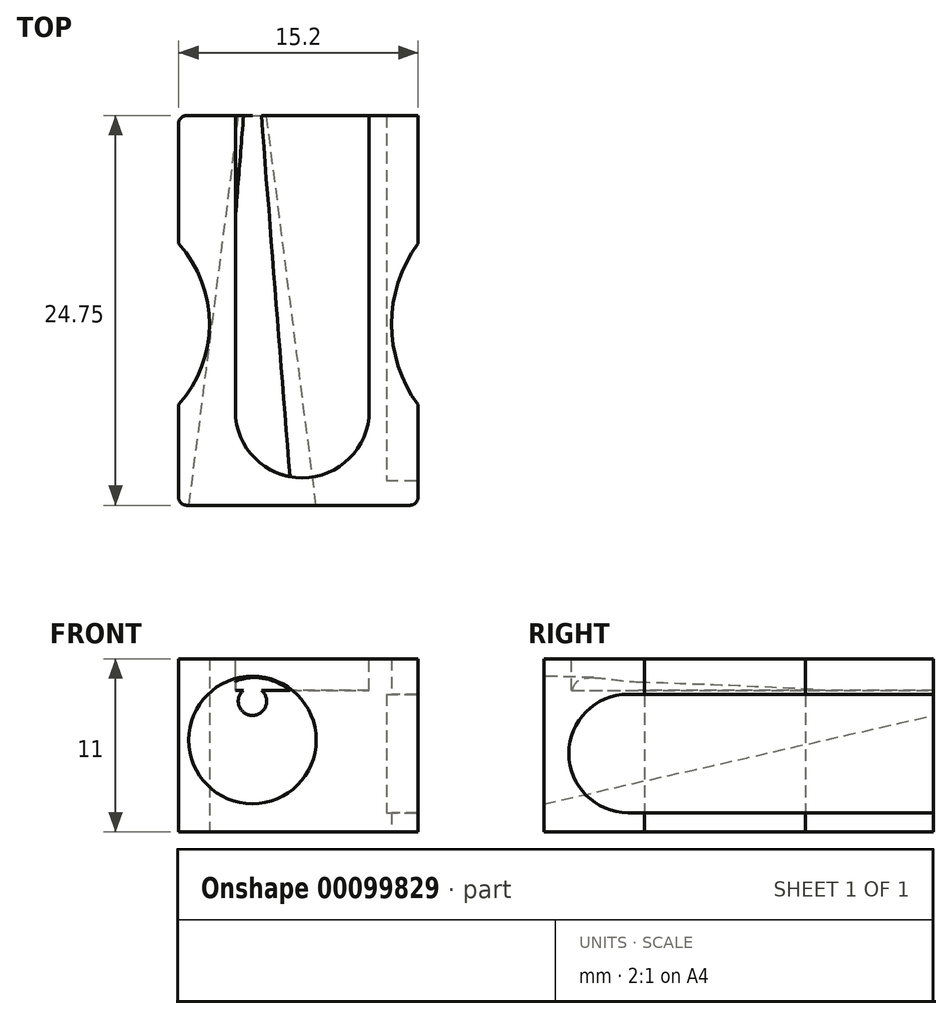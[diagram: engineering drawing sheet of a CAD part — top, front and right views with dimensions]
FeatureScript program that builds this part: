
annotation { "Feature Type Name" : "Feature", "Feature Type Description" : "" }
export const myFeature = defineFeature(function(context is Context, id is Id, definition is map)
    precondition{}
    {
        {
            var Q0;
            Q0=qCreatedBy(makeId("Top.planeOp"),FACE);
            var sketch = newSketch(context, id + "F0", { "sketchPlane" : qUnion([Q0])});
            skLineSegment(sketch, "E0", {"start": v(-7.6, 0) * mm, "end": v(7.6, 0) * mm});
            skLineSegment(sketch, "E1", {"start": v(7.6, 24.75) * mm, "end": v(-7.6, 24.75) * mm});
            skArc(sketch, "E2", {"start": v(7.6, 16.6) * mm, "mid": v(5.93, 11.5) * mm, "end": v(7.6, 6.4) * mm});
            skArc(sketch, "E3", {"start": v(-7.6, 6.4) * mm, "mid": v(-5.65, 11.5) * mm, "end": v(-7.6, 16.6) * mm});
            skLineSegment(sketch, "E4", {"start": v(-7.6, 24.75) * mm, "end": v(-7.6, 16.6) * mm});
            skLineSegment(sketch, "E5", {"start": v(-7.6, 6.4) * mm, "end": v(-7.6, 0) * mm});
            skLineSegment(sketch, "E6", {"start": v(7.6, 24.75) * mm, "end": v(7.6, 16.6) * mm});
            skLineSegment(sketch, "E7", {"start": v(7.6, 6.4) * mm, "end": v(7.6, 0) * mm});
            skSolve(sketch);
        }
        {
            var Q0;
            Q0 = qSketchRegion(id + "F0", true);
            var Q1;
            Q1=makeQuery(id+"F0.imprint","IMPRINT",FACE,{"disambiguationData":[TD([[makeQuery(id+"F0.imprint","IMPRINT",EDGE,{"derivedFrom":sQuery(id+"F0.wireOp",EDGE,"E0")}),1.0]])]});
            extrude(context, id + "F1", {"entities" : qUnion([Q0, Q1]), "depth" : 11 * mm});
        }
        {
            var Q0;
            Q0=makeQuery(id+"F1.opExtrude","CAP_FACE",FACE,{"disambiguationData":[OSD([sQuery(id+"F0.wireOp",EDGE,"E0"),sQuery(id+"F0.wireOp",EDGE,"CH1Bz3xv-YDNb-fB7E-m70Z-ND1As7hxYgC0"),sQuery(id+"F0.wireOp",EDGE,"E1"),sQuery(id+"F0.wireOp",EDGE,"xgEUE1xi-ovgt-coFG-tonh-Vv3ERaxNFuPz")])],"isStart":false});
            var sketch = newSketch(context, id + "F2", { "sketchPlane" : qUnion([Q0])});
            skLineSegment(sketch, "E8", {"start": v(-4, 24.75) * mm, "end": v(-4, 6) * mm});
            skLineSegment(sketch, "E9", {"start": v(4.5, 24.75) * mm, "end": v(4.5, 6) * mm});
            skArc(sketch, "E10", {"start": v(-4, 6) * mm, "mid": v(0.25, 1.74) * mm, "end": v(4.5, 6) * mm});
            skSolve(sketch);
        }
        {
            var Q0;
            {var subQ0=sQuery(id+"F2.wireOp",EDGE,"E8");Q0=makeQuery(id+"F2.imprint","IMPRINT",FACE,{"disambiguationData":[TD([[makeQuery(id+"F2.imprint","IMPRINT",EDGE,{"derivedFrom":subQ0}),1.0]])]});}
            extrude(context, id + "F3", {"entities" : qUnion([Q0]), "operationType" : NewBodyOperationType.REMOVE, "oppositeDirection" : true, "depth" : 2 * mm});
        }
        {
            var Q0;
            Q0=qCreatedBy(makeId("Front.planeOp"),FACE);
            cPlane(context, id + "F4", {"entities" : qUnion([Q0]), "cplaneType" : CPlaneType.OFFSET, "offset" : 24.75 * mm, "oppositeDirection" : true, "width" : 150 * mm, "height" : 150 * mm});
        }
        {
            var Q0;
            Q0=makeQuery(id+"F1.opExtrude","SWEPT_FACE",FACE,{"disambiguationData":[OSD([sQuery(id+"F0.wireOp",EDGE,"E0")])]});
            var sketch = newSketch(context, id + "F5", { "sketchPlane" : qUnion([Q0])});
            skCircle(sketch, "E11", {"center": v(-2.91, 5.84) * mm, "radius": 4.05 * mm});
            skSolve(sketch);
        }
        {
            var Q0;
            Q0=qCreatedBy(id+"F4.planeOp",FACE);
            var sketch = newSketch(context, id + "F6", { "sketchPlane" : qUnion([Q0])});
            skCircle(sketch, "E12", {"center": v(-2.91, 8.3) * mm, "radius": 0.9 * mm});
            skSolve(sketch);
        }
        {
            var Q1;
            Q1=makeQuery(id+"F5.imprint","IMPRINT",FACE,{"disambiguationData":[TD([[makeQuery(id+"F5.imprint","IMPRINT",EDGE,{"derivedFrom":sQuery(id+"F5.wireOp",EDGE,"E11")}),1.0]])]});
            var Q2;
            Q2=makeQuery(id+"F6.imprint","IMPRINT",FACE,{"disambiguationData":[TD([[makeQuery(id+"F6.imprint","IMPRINT",EDGE,{"derivedFrom":sQuery(id+"F6.wireOp",EDGE,"E12")}),1.0]])]});
            loft(context, id + "F7", {"operationType" : NewBodyOperationType.REMOVE, "sheetProfilesArray" : [{ "sheetProfileEntities" : qUnion([Q1]) }, { "sheetProfileEntities" : qUnion([Q2]) }]});
        }
        {
            var Q0;
            Q0=makeQuery(id+"F1.opExtrude","SWEPT_EDGE",EDGE,{"disambiguationData":[OSD([sQuery(id+"F0.wireOp",EDGE,"E0"),sQuery(id+"F0.wireOp",EDGE,"E5")])]});
            var Q1;
            Q1=makeQuery(id+"F1.opExtrude","SWEPT_EDGE",EDGE,{"disambiguationData":[OSD([sQuery(id+"F0.wireOp",EDGE,"E1"),sQuery(id+"F0.wireOp",EDGE,"E4")])]});
            var Q2;
            Q2=makeQuery(id+"F1.opExtrude","SWEPT_EDGE",EDGE,{"disambiguationData":[OSD([sQuery(id+"F0.wireOp",EDGE,"E0"),sQuery(id+"F0.wireOp",EDGE,"E7")])]});
            fillet(context, id + "F8", {"entities" : qUnion([Q0, Q1, Q2]), "radius" : 0.5 * mm, "tangentPropagation" : true, "allowEdgeOverflow" : false});
        }
        {
            var Q0;
            Q0=makeQuery(id+"F1.opExtrude","SWEPT_FACE",FACE,{"disambiguationData":[OSD([sQuery(id+"F0.wireOp",EDGE,"E6"),sQuery(id+"F0.wireOp",EDGE,"E7"),sQuery(id+"F0.wireOp",EDGE,"jYAzOSRn-kvyj-A9Oq-DmZ8-IOtMs528JoDm")])]});
            var sketch = newSketch(context, id + "F9", { "sketchPlane" : qUnion([Q0])});
            skLineSegment(sketch, "E13", {"start": v(24.75, 1.22) * mm, "end": v(5.34, 1.22) * mm});
            skArc(sketch, "E14", {"start": v(5.34, 8.74) * mm, "mid": v(1.58, 4.98) * mm, "end": v(5.34, 1.22) * mm});
            skLineSegment(sketch, "E15", {"start": v(5.34, 8.74) * mm, "end": v(24.75, 8.74) * mm});
            skSolve(sketch);
        }
        {
            var Q0;
            Q0 = qSketchRegion(id + "F9", true);
            var Q1;
            {var subQ0=sQuery(id+"F9.wireOp",EDGE,"E13");Q1=makeQuery(id+"F9.imprint","IMPRINT",FACE,{"disambiguationData":[TD([[makeQuery(id+"F9.imprint","IMPRINT",EDGE,{"derivedFrom":subQ0}),-1.0]])]});}
            extrude(context, id + "F10", {"entities" : qUnion([Q0, Q1]), "operationType" : NewBodyOperationType.REMOVE, "oppositeDirection" : true, "depth" : 2 * mm});
        }
    });
